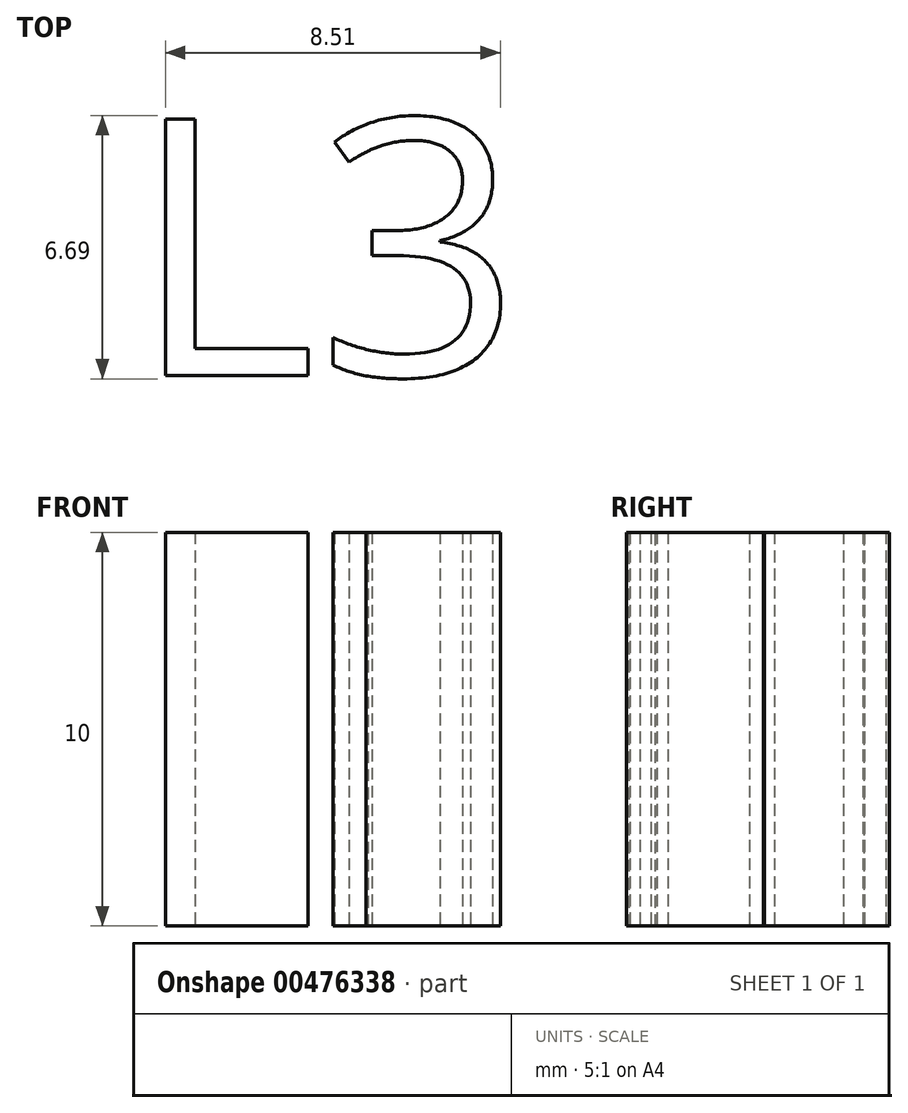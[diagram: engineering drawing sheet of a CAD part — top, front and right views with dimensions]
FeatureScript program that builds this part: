
annotation { "Feature Type Name" : "Feature", "Feature Type Description" : "" }
export const myFeature = defineFeature(function(context is Context, id is Id, definition is map)
    precondition{}
    {
        {
            var Q0;
            Q0=qCreatedBy(makeId("Top.planeOp"),FACE);
            var sketch = newSketch(context, id + "F0", { "sketchPlane" : qUnion([Q0])});
            skText(sketch, "E0", { "text": "L3", "fontName": "OpenSans-Regular.ttf"});
            skLineSegment(sketch, "E1", {"start": v(-5, 0) * mm, "end": v(5, 0) * mm, "construction": true});
            skPoint(sketch, "E1.endSnap0", {"position": v(5, 0) * mm});
            skLineSegment(sketch, "E2", {"start": v(0, 3.28) * mm, "end": v(0, -3.28) * mm, "construction": true});
            const initialGuessF0  = {"E0": [-0.005, -0.00328, 1, 0, 0.00656]};
            skSetInitialGuess(sketch, initialGuessF0);
            skSolve(sketch);
        }
        {
            var Q0;
            Q0 = qSketchRegion(id + "F0", true);
            extrude(context, id + "F1", {"entities" : qUnion([Q0]), "depth" : 10 * mm});
        }
    });
